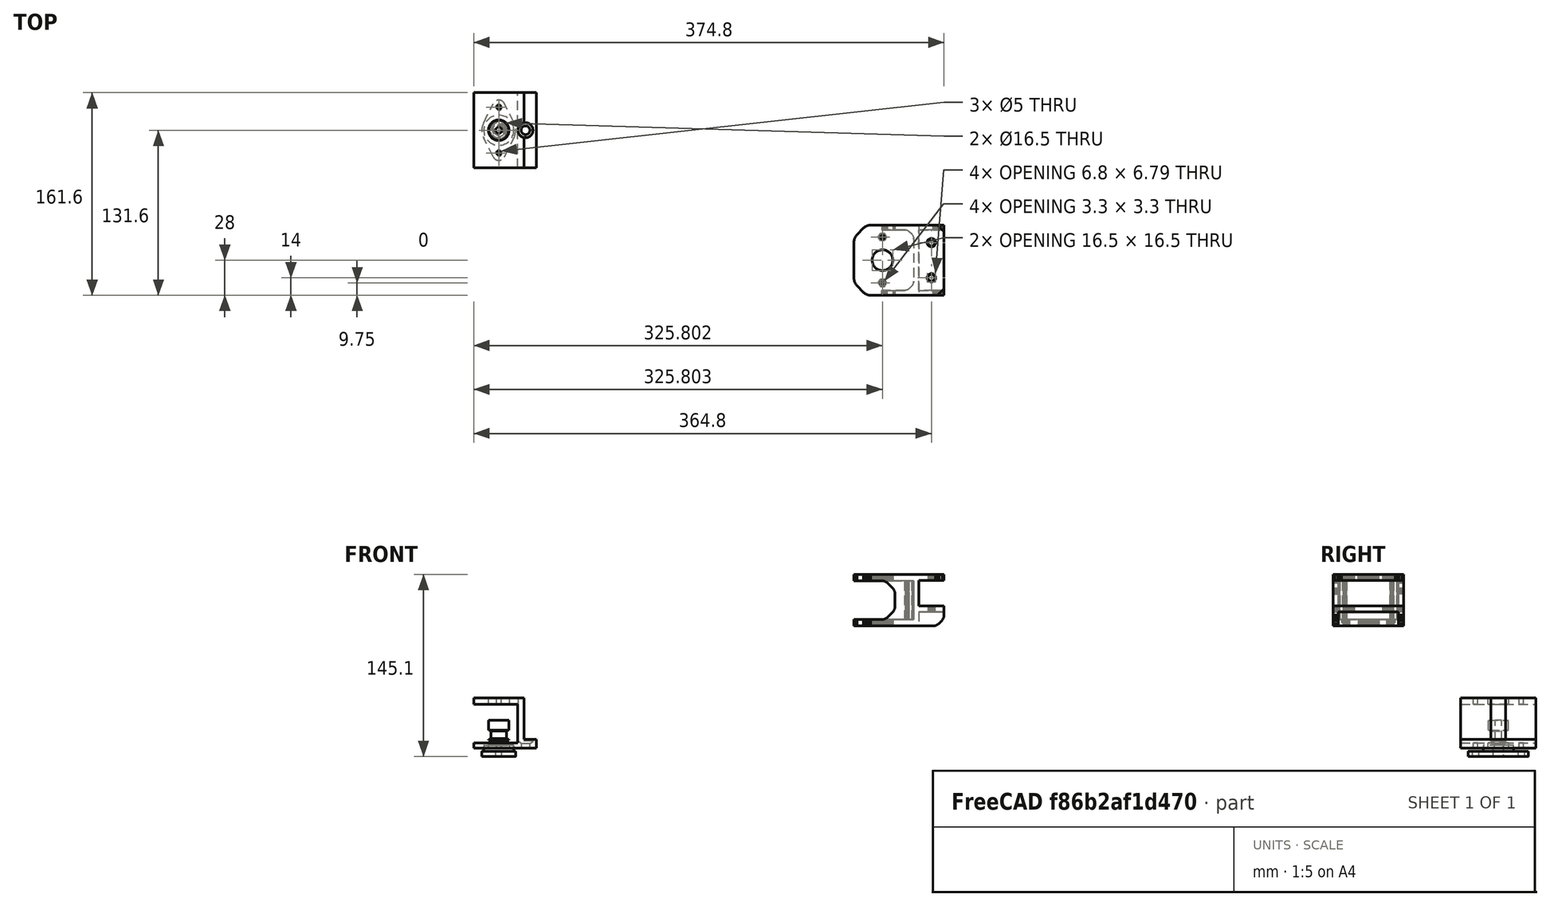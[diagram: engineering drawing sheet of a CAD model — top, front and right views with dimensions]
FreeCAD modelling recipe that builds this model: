
FCSTD DOCUMENT  (FreeCAD 0.17R10423 (Git))
Label: zbearing
License: All rights reserved
LicenseURL: http://en.wikipedia.org/wiki/All_rights_reserved
objects: App::FeaturePython×8, Sketcher::SketchObject×7, PartDesign::Pocket×5, Part::Feature×3, PartDesign::Pad×2, Part::FeaturePython×2, Mesh::Feature×1, PartDesign::Chamfer×1, PartDesign::Body×1
note: 28 computed .brp shape members not serialized (recipe doc carries the construction recipe); baked Part::Feature solids carry a one-line shape summary decoded from their .brp

FEATURE [Mesh::Feature] Leadscrew_Pulley_Bearing_Mount  label="Leadscrew_Pulley-Bearing_Mount"
FEATURE [Part::Feature] Leadscrew_Pulley_Bearing_Mount001
  shape: bbox 71.66 x 56 x 41 mm, 4754 faces, 0 solids (baked)
FEATURE [Part::Feature] Leadscrew_Pulley_Bearing_Mount001_solid  label="Leadscrew_Pulley_Bearing_Mount001 (Solid)"
  shape: bbox 71.66 x 56 x 41 mm, 4754 faces (baked)
FEATURE [Part::Feature] Leadscrew_Pulley_Bearing_Mount001_solid001  label="Leadscrew_Pulley_Bearing_Mount001 (Solid)001"
  shape: bbox 71.66 x 56 x 41 mm, 1916 faces (baked)
FEATURE [Sketcher::SketchObject] Sketch
  MapMode = 5
  Placement = pos=(0,0,118.6) rot=(0,0,1;0rad)
  sketch-geometry (3):
    g0: Circle CenterX=0 CenterY=0 CenterZ=0 NormalX=0 NormalY=0 NormalZ=1 Radius=8.25
    g1: Circle CenterX=0 CenterY=-18.25 CenterZ=0 NormalX=0 NormalY=0 NormalZ=1 Radius=1.65
    g2: Circle CenterX=0 CenterY=18.25 CenterZ=0 NormalX=0 NormalY=0 NormalZ=1 Radius=1.65
  constraints (8):
    c: DistanceY(g0,g2) = 18.25
    c: DistanceY(g1,g0) = 18.25
    c: Radius(g0) = 8.25
    c: Radius(g2) = 1.65
    c: Equal(g2,g1)
    c: DistanceX(g2,g0) = 0
    c: DistanceX(g1,g0) = 0
    c: Coincident(g0,g-1)
FEATURE [Sketcher::SketchObject] Sketch001
  MapMode = 5
  Support = -> [XY_Plane]
  sketch-geometry (4):
    g0: LineSegment StartX=-20 StartY=30 StartZ=0 EndX=20 EndY=30 EndZ=0
    g1: LineSegment StartX=20 StartY=30 StartZ=0 EndX=20 EndY=-30 EndZ=0
    g2: LineSegment StartX=20 StartY=-30 StartZ=0 EndX=-20 EndY=-30 EndZ=0
    g3: LineSegment StartX=-20 StartY=-30 StartZ=0 EndX=-20 EndY=30 EndZ=0
  constraints (11):
    c: Coincident(g0,g1)
    c: Coincident(g1,g2)
    c: Coincident(g2,g3)
    c: Coincident(g3,g0)
    c: Horizontal(g0)
    c: Horizontal(g2)
    c: Vertical(g1)
    c: Vertical(g3)
    c: DistanceY(g1,g1) = 60
    c: DistanceX(g0,g0) = 40
    c: Symmetric(g0,g1,g-1)
FEATURE [PartDesign::Pad] Pad
  Length = 40
  Length2 = 100
  Midplane = true
  Profile = -> Sketch001
  Type = 0
FEATURE [PartDesign::Pocket] Pocket
  BaseFeature = -> Pad
  Length = 5
  Midplane = true
  Profile = -> Sketch
  Type = 1
FEATURE [Sketcher::SketchObject] Sketch002
  ExternalGeometry = -> [Pocket]
  MapMode = 5
  Placement = pos=(0,0,0) rot=(1,0,0;1.5708rad)
  Support = -> [XZ_Plane]
  sketch-geometry (4):
    g0: LineSegment StartX=-20 StartY=15.1393 StartZ=0 EndX=15 EndY=15.1393 EndZ=0
    g1: LineSegment StartX=15 StartY=15.1393 StartZ=0 EndX=15 EndY=-15.8607 EndZ=0
    g2: LineSegment StartX=15 StartY=-15.8607 StartZ=0 EndX=-20 EndY=-15.8607 EndZ=0
    g3: LineSegment StartX=-20 StartY=-15.8607 StartZ=0 EndX=-20 EndY=15.1393 EndZ=0
  constraints (11):
    c: Coincident(g0,g1)
    c: Coincident(g1,g2)
    c: Coincident(g2,g3)
    c: Coincident(g3,g0)
    c: Horizontal(g0)
    c: Horizontal(g2)
    c: Vertical(g1)
    c: Vertical(g3)
    c: DistanceY(g3,g3) = 31
    c: DistanceX(g0,g-3) = 0
    c: DistanceX(g0,g-4) = 5
FEATURE [PartDesign::Pocket] Pocket001
  BaseFeature = -> Pocket
  Length = 5
  Midplane = true
  Profile = -> Sketch002
  Type = 1
FEATURE [Sketcher::SketchObject] Sketch003
  ExternalGeometry = -> [Pocket001]
  MapMode = 5
  Placement = pos=(20,0,0) rot=(0.57735,0.57735,0.57735;2.0944rad)
  Support = -> [Pocket001]
  sketch-geometry (4):
    g0: LineSegment StartX=-30 StartY=-20 StartZ=0 EndX=30 EndY=-20 EndZ=0
    g1: LineSegment StartX=30 StartY=-20 StartZ=0 EndX=30 EndY=-13 EndZ=0
    g2: LineSegment StartX=30 StartY=-13 StartZ=0 EndX=-30 EndY=-13 EndZ=0
    g3: LineSegment StartX=-30 StartY=-13 StartZ=0 EndX=-30 EndY=-20 EndZ=0
  constraints (11):
    c: Coincident(g0,g1)
    c: Coincident(g1,g2)
    c: Coincident(g2,g3)
    c: Coincident(g3,g0)
    c: Horizontal(g0)
    c: Horizontal(g2)
    c: Vertical(g1)
    c: Vertical(g3)
    c: Coincident(g0,g-3)
    c: Coincident(g0,g-3)
    c: DistanceY(g3,g3) = 7
FEATURE [PartDesign::Pad] Pad001
  BaseFeature = -> Pocket001
  Length = 10
  Length2 = 100
  Profile = -> Sketch003
  Type = 0
FEATURE [Sketcher::SketchObject] Sketch004
  MapMode = 5
  Placement = pos=(0,0,-20) rot=(1,0,0;3.14159rad)
  Support = -> [Pad001]
  sketch-geometry (1):
    g0: Circle CenterX=21.3 CenterY=0 CenterZ=0 NormalX=0 NormalY=0 NormalZ=1 Radius=3.5
  constraints (3):
    c: PointOnObject(g0,g-1)
    c: DistanceX(g-1,g0) = 21.3
    c: Radius(g0) = 3.5
FEATURE [PartDesign::Pocket] Pocket002
  BaseFeature = -> Pad001
  Length = 5
  Profile = -> Sketch004
  Type = 1
FEATURE [Sketcher::SketchObject] Sketch005
  ExternalGeometry = -> [Pocket002]
  MapMode = 5
  Placement = pos=(0,0,-13) rot=(0,0,1;0rad)
  Support = -> [Pocket002]
  sketch-geometry (1):
    g0: Circle CenterX=21.3 CenterY=0 CenterZ=0 NormalX=0 NormalY=0 NormalZ=1 Radius=6
  constraints (2):
    c: Coincident(g0,g-3)
    c: Radius(g0) = 6
FEATURE [PartDesign::Pocket] Pocket003
  BaseFeature = -> Pocket002
  Length = 1
  Profile = -> Sketch005
  Reversed = true
  Type = 1
FEATURE [Sketcher::SketchObject] Sketch006
  ExternalGeometry = -> [Pocket003]
  MapMode = 5
  Placement = pos=(0,0,-13) rot=(0,0,1;0rad)
  Support = -> [Pocket003]
  sketch-geometry (1):
    g0: Circle CenterX=21.3 CenterY=0 CenterZ=0 NormalX=0 NormalY=0 NormalZ=1 Radius=6
  constraints (2):
    c: Coincident(g0,g-3)
    c: Radius(g0) = 6
FEATURE [PartDesign::Pocket] Pocket004
  BaseFeature = -> Pocket003
  Length = 1
  Profile = -> Sketch006
  Type = 0
FEATURE [PartDesign::Chamfer] Chamfer
  Base = -> Pocket004 [Edge37]
  BaseFeature = -> Pocket004
  Placement = pos=(0,0,-10.6393) rot=(0,0,1;0rad)
  Size = 2.49
FEATURE [PartDesign::Body] Body
  Group = -> [Sketch,Sketch001,Pad,Pocket,Sketch002,Pocket001,Sketch003,Pad001,Sketch004,Pocket002,Sketch005,Pocket003,Sketch006,Pocket004,Chamfer]
  Origin = -> BodyOrigin
  Tip = -> Chamfer
FEATURE [Part::FeaturePython] gt2_pulley_01  # a2plus imported part (geometry in sourceFile) (typed FeaturePython)
  Placement = pos=(-5e-12,0,-5.5) rot=(-0.57735,-0.57735,0.57735;2.0944rad)
  fixedPosition = false
  sourceFile = <path>
  timeLastImport = 1.48904e+09
  updateColors = true
FEATURE [Part::FeaturePython] kfl08_01  # a2plus imported part (geometry in sourceFile) (typed FeaturePython)
  Placement = pos=(0,0,-26.5) rot=(0,0,1;1.5708rad)
  fixedPosition = false
  sourceFile = <path>
  timeLastImport = 1.48912e+09
  updateColors = true
FEATURE [App::FeaturePython] axialConstraint01  label="axialConstraint01__kfl08_01"  # a2plus constraint (typed FeaturePython)
  Object1 = Chamfer
  Object2 = kfl08_01
  SubElement1 = Face13
  SubElement2 = Face17
  Type = axial
  directionConstraint = 0
  lockRotation = false
FEATURE [App::FeaturePython] axialConstraint01_mirror  label="axialConstraint01__Chamfer"  # a2plus constraint (typed FeaturePython)
  Object1 = Chamfer
  Object2 = kfl08_01
  SubElement1 = Face13
  SubElement2 = Face17
  Type = axial
  directionConstraint = 0
  lockRotation = false
FEATURE [App::FeaturePython] planeConstraint01  label="planeConstraint01__Chamfer"  # a2plus constraint (typed FeaturePython)
  Object1 = kfl08_01
  Object2 = Chamfer
  SubElement1 = Face4
  SubElement2 = Face17
  Type = plane
  directionConstraint = 0
  offset = 0
FEATURE [App::FeaturePython] planeConstraint01_mirror  label="planeConstraint01__kfl08_01"  # a2plus constraint (typed FeaturePython)
  Object1 = kfl08_01
  Object2 = Chamfer
  SubElement1 = Face4
  SubElement2 = Face17
  Type = plane
  directionConstraint = 0
  offset = 0
FEATURE [App::FeaturePython] planeConstraint02  label="planeConstraint02__kfl08_01"  # a2plus constraint (typed FeaturePython)
  Object1 = gt2_pulley_01
  Object2 = kfl08_01
  SubElement1 = Face9
  SubElement2 = Face19
  Type = plane
  directionConstraint = 1
  offset = 0
FEATURE [App::FeaturePython] planeConstraint02_mirror  label="planeConstraint02__gt2_pulley_01"  # a2plus constraint (typed FeaturePython)
  Object1 = gt2_pulley_01
  Object2 = kfl08_01
  SubElement1 = Face9
  SubElement2 = Face19
  Type = plane
  directionConstraint = 1
  offset = 0
FEATURE [App::FeaturePython] axialConstraint02  label="axialConstraint02__gt2_pulley_01"  # a2plus constraint (typed FeaturePython)
  Object1 = kfl08_01
  Object2 = gt2_pulley_01
  SubElement1 = Face17
  SubElement2 = Face6
  Type = axial
  directionConstraint = 1
  lockRotation = false
FEATURE [App::FeaturePython] axialConstraint02_mirror  label="axialConstraint02__kfl08_01"  # a2plus constraint (typed FeaturePython)
  Object1 = kfl08_01
  Object2 = gt2_pulley_01
  SubElement1 = Face17
  SubElement2 = Face6
  Type = axial
  directionConstraint = 1
  lockRotation = false
note: 2 file-system paths scrubbed to <path> (originals preserved in the JSON sidecar)
